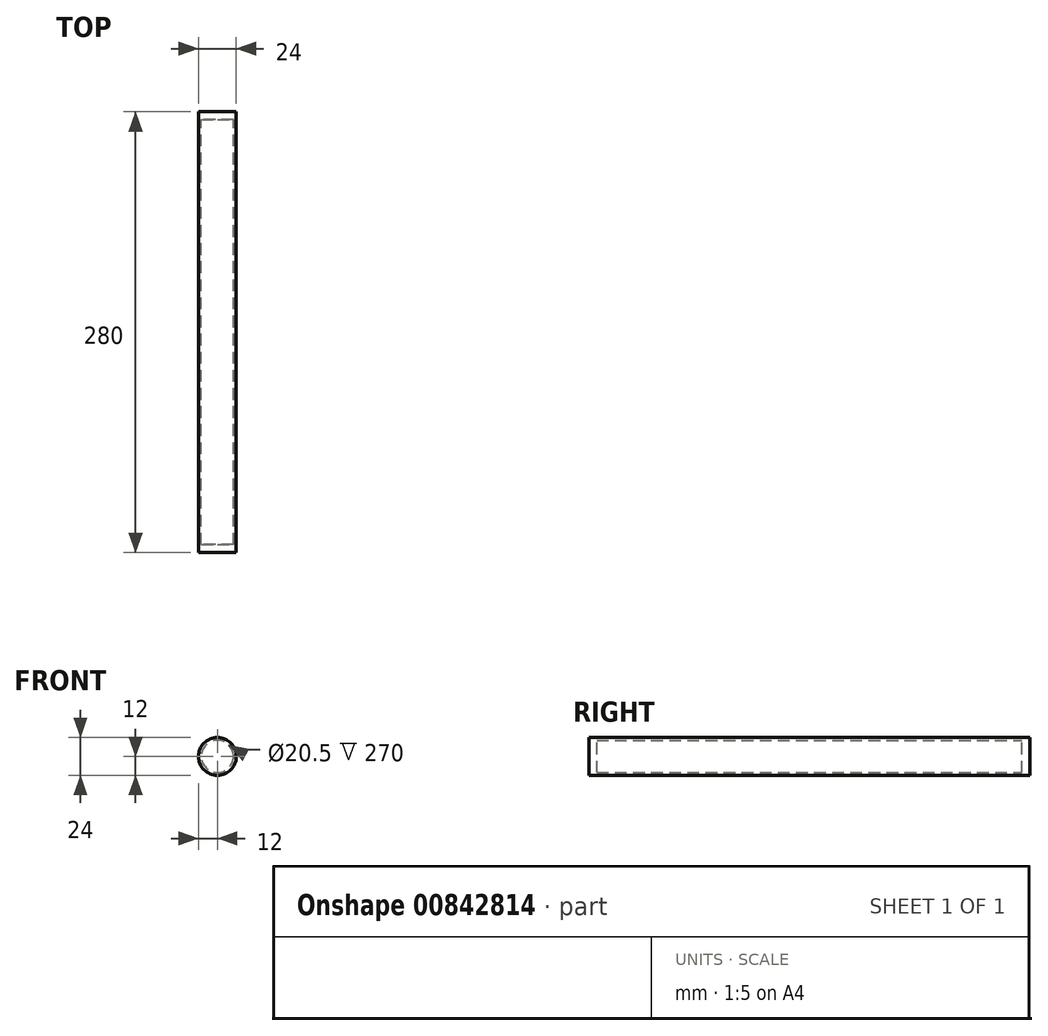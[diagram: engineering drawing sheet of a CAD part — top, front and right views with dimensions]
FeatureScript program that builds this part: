
annotation { "Feature Type Name" : "Feature", "Feature Type Description" : "" }
export const myFeature = defineFeature(function(context is Context, id is Id, definition is map)
    precondition{}
    {
        {
            var Q0;
            Q0=qCreatedBy(makeId("Front.planeOp"),FACE);
            var sketch = newSketch(context, id + "F0", { "sketchPlane" : qUnion([Q0])});
            skCircle(sketch, "E0", {"center": v(0, 0) * mm, "radius": 10.25 * mm});
            skCircle(sketch, "E1", {"center": v(0, 0) * mm, "radius": 12 * mm});
            skSolve(sketch);
        }
        {
            var Q0;
            Q0=makeQuery(id+"F0.imprint","IMPRINT",FACE,{"disambiguationData":[TD([[makeQuery(id+"F0.imprint","IMPRINT",EDGE,{"derivedFrom":sQuery(id+"F0.wireOp",EDGE,"E0")}),-1.0]])]});
            extrude(context, id + "F1", {"entities" : qUnion([Q0]), "depth" : 270 * mm, "offsetDistance" : 25 * mm});
        }
        {
            var Q0;
            Q0=makeQuery(id+"F1.opExtrude","CAP_FACE",FACE,{"disambiguationData":[OSD([sQuery(id+"F0.wireOp",EDGE,"E0"),sQuery(id+"F0.wireOp",EDGE,"E1")])],"isStart":false});
            var sketch = newSketch(context, id + "F2", { "sketchPlane" : qUnion([Q0])});
            skCircle(sketch, "E2", {"center": v(0, 0) * mm, "radius": 12 * mm});
            skSolve(sketch);
        }
        {
            var Q0;
            Q0 = qSketchRegion(id + "F2", true);
            extrude(context, id + "F3", {"entities" : qUnion([Q0]), "operationType" : NewBodyOperationType.ADD, "depth" : 5 * mm, "offsetDistance" : 25 * mm});
        }
        {
            var Q0;
            Q0=makeQuery(id+"F1.opExtrude","CAP_FACE",FACE,{"disambiguationData":[OSD([sQuery(id+"F0.wireOp",EDGE,"E0"),sQuery(id+"F0.wireOp",EDGE,"E1")])],"isStart":true});
            var sketch = newSketch(context, id + "F4", { "sketchPlane" : qUnion([Q0])});
            skCircle(sketch, "E3", {"center": v(0, 0) * mm, "radius": 12 * mm});
            skSolve(sketch);
        }
        {
            var Q0;
            Q0 = qSketchRegion(id + "F4", true);
            extrude(context, id + "F5", {"entities" : qUnion([Q0]), "operationType" : NewBodyOperationType.ADD, "depth" : 5 * mm, "offsetDistance" : 25 * mm});
        }
    });
